# Revit family: Pipe_Cover-Navien-NPE-2
name_source: partatom
category: Mechanical Equipment
units: mm (PartAtom-declared; Revit-internal decimal feet)

## family parameters
Cut with Voids When Loaded = No
Host = Face
OmniClass Number = 23.65.35.11
OmniClass Title = Supply Water Heaters
Part Type = Normal
Room Calculation Point = No
Round Connector Dimension = Use Diameter
Shared = No

## types (1)
- Pipe Cover for NPE-2 Series
    Assembly Code = D
    Default Elevation = 48 "
    Depth = 13.6 "
    Description = Pipe cover designed to hide gas, water and power lines for an elegant, clean look. Works with NPE-2 series units. Use with 30012581A Plumb Easy Valve Kit.
    Finish = Metal - Navien - White
    Height = 17.5 "
    Installation Type = Pipe Cover - Wall Mounted
    Keynote = Division 22
    Manufacturer = Navien, Inc.
    Manufacturer Fax Number = (949) 420-0430
    Model = 30025812A
    Product Documentation Link = https://www.navieninc.com
    Product Name = Pipe Cover for NPE-2 Series
    Product Page URL = https://www.navieninc.com
    URL = https://www.navieninc.com
    Version = 2019 - v1.0a
    Warranty = https://www.navieninc.com
    Weight = 0.00 lbf
    Width = 17.3 "

## geometry (parser evidence)
native form markers: Sweep x3
no freeform markers — native parametric forms only
